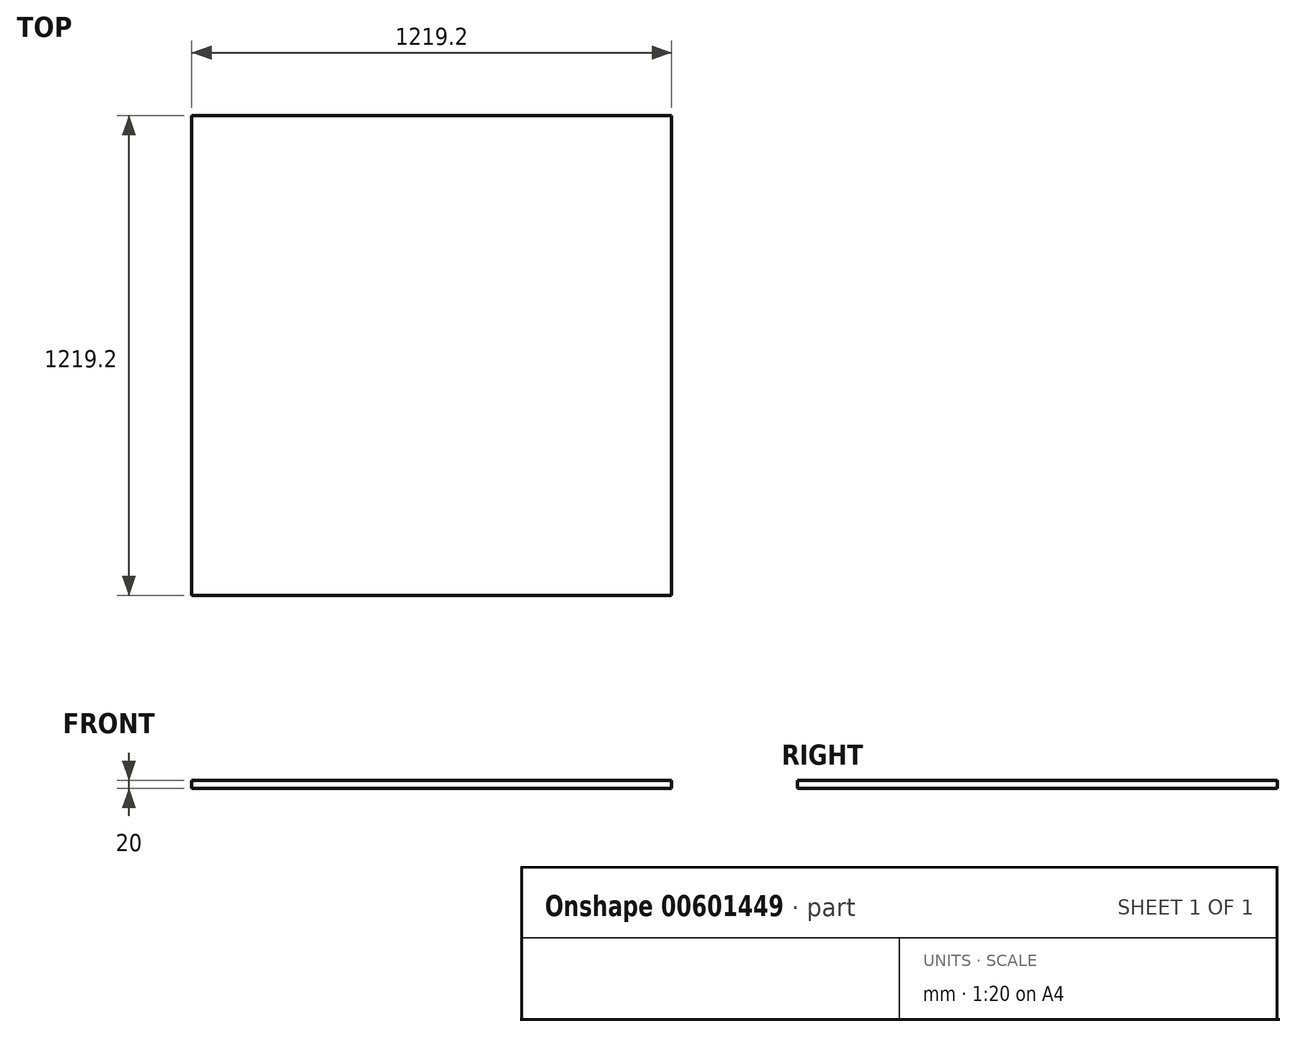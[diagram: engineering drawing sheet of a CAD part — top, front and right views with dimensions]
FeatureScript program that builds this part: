
annotation { "Feature Type Name" : "Feature", "Feature Type Description" : "" }
export const myFeature = defineFeature(function(context is Context, id is Id, definition is map)
    precondition{}
    {
        {
            var Q0;
            Q0=qCreatedBy(makeId("Top.planeOp"),FACE);
            var sketch = newSketch(context, id + "F0", { "sketchPlane" : qUnion([Q0])});
            skLineSegment(sketch, "E0.bottom", {"start": v(0, 0) * mm, "end": v(1219.2, 0) * mm});
            skLineSegment(sketch, "E0.top", {"start": v(0, 1219.2) * mm, "end": v(1219.2, 1219.2) * mm});
            skLineSegment(sketch, "E0.left", {"start": v(0, 0) * mm, "end": v(0, 1219.2) * mm});
            skLineSegment(sketch, "E0.right", {"start": v(1219.2, 0) * mm, "end": v(1219.2, 1219.2) * mm});
            skSolve(sketch);
        }
        {
            var Q0;
            Q0 = qSketchRegion(id + "F0", true);
            extrude(context, id + "F1", {"entities" : qUnion([Q0]), "depth" : 20 * mm, "offsetDistance" : 25.4 * mm});
        }
    });
